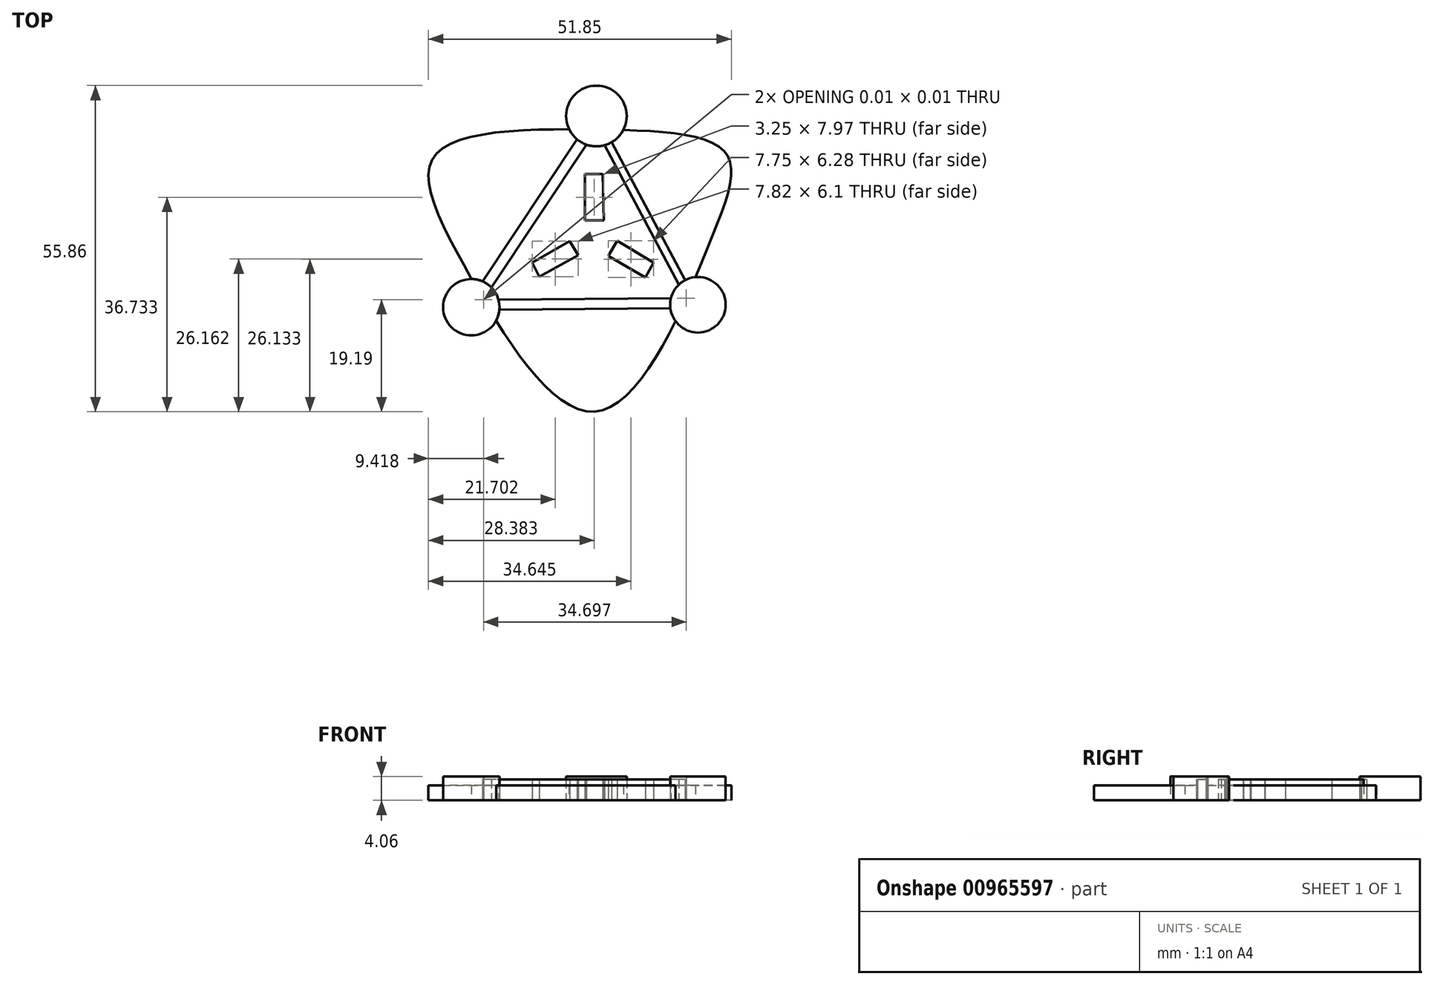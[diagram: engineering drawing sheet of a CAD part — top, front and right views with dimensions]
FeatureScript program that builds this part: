
annotation { "Feature Type Name" : "Feature", "Feature Type Description" : "" }
export const myFeature = defineFeature(function(context is Context, id is Id, definition is map)
    precondition{}
    {
        {
            var Q0;
            Q0=qCreatedBy(makeId("Top.planeOp"),FACE);
            var sketch = newSketch(context, id + "F0", { "sketchPlane" : qUnion([Q0])});
            skFitSpline(sketch, "E0", {"points": [v(-33.67, 21.37) * mm, v(-6.09, 25.74) * mm, v(15.95, 21.83) * mm, v(13.28, 6.3) * mm, v(-6.1, -22.56) * mm, v(-28.52, 2.03) * mm, v(-33.67, 21.37) * mm]});
            skLineSegment(sketch, "E1", {"start": v(-6.09, 25.74) * mm, "end": v(-25.43, -3.42) * mm});
            skLineSegment(sketch, "E2", {"start": v(9.28, -3.15) * mm, "end": v(-6.09, 25.74) * mm});
            skLineSegment(sketch, "E3", {"start": v(-25.43, -3.42) * mm, "end": v(9.28, -3.15) * mm});
            skCircle(sketch, "E4", {"center": v(-6.09, 28.06) * mm, "radius": 5.2 * mm});
            skCircle(sketch, "E5", {"center": v(11.28, -4.28) * mm, "radius": 4.76 * mm});
            skCircle(sketch, "E6", {"center": v(-27.5, -4.7) * mm, "radius": 4.83 * mm});
            skLineSegment(sketch, "E7", {"start": v(-8.08, 18.12) * mm, "end": v(-8.08, 10.15) * mm});
            skLineSegment(sketch, "E8", {"start": v(-8.08, 10.15) * mm, "end": v(-4.83, 10.15) * mm});
            skLineSegment(sketch, "E9", {"start": v(-4.83, 10.15) * mm, "end": v(-5, 18.09) * mm});
            skLineSegment(sketch, "E10", {"start": v(-5, 18.09) * mm, "end": v(-8.08, 18.12) * mm});
            skLineSegment(sketch, "E11", {"start": v(-17.05, 2.95) * mm, "end": v(-10.66, 6.61) * mm});
            skLineSegment(sketch, "E12", {"start": v(-10.66, 6.61) * mm, "end": v(-9.23, 4.24) * mm});
            skLineSegment(sketch, "E13", {"start": v(-9.23, 4.24) * mm, "end": v(-15.87, 0.51) * mm});
            skLineSegment(sketch, "E14", {"start": v(-15.87, 0.51) * mm, "end": v(-17.05, 2.95) * mm});
            skLineSegment(sketch, "E15", {"start": v(-2.56, 6.67) * mm, "end": v(-4.07, 4.1) * mm});
            skLineSegment(sketch, "E16", {"start": v(-4.07, 4.1) * mm, "end": v(2.26, 0.4) * mm});
            skLineSegment(sketch, "E17", {"start": v(2.26, 0.4) * mm, "end": v(3.68, 2.96) * mm});
            skLineSegment(sketch, "E18", {"start": v(3.68, 2.96) * mm, "end": v(-2.56, 6.67) * mm});
            skLineSegment(sketch, "E19", {"start": v(-8.28, 25.76) * mm, "end": v(-26.46, -1.63) * mm});
            skLineSegment(sketch, "E20", {"start": v(-26.46, -1.63) * mm, "end": v(-24.42, -5.12) * mm});
            skLineSegment(sketch, "E21", {"start": v(-24.42, -5.12) * mm, "end": v(8.5, -4.86) * mm});
            skLineSegment(sketch, "E22", {"start": v(8.5, -4.86) * mm, "end": v(9.95, -1.63) * mm});
            skLineSegment(sketch, "E23", {"start": v(9.95, -1.63) * mm, "end": v(-3.46, 23.57) * mm});
            skSolve(sketch);
        }
        {
            var Q0;
            Q0=makeQuery(id+"F0.imprint","IMPRINT",FACE,{"disambiguationData":[TD([[makeQuery(id+"F0.imprint","IMPRINT",EDGE,{"derivedFrom":sQuery(id+"F0.wireOp",EDGE,"E7")}),-1.0]])]});
            var Q1;
            {var subQ1=sQuery(id+"F0.wireOp",EDGE,"E2");var subQ3=sQuery(id+"F0.wireOp",EDGE,"E5");var subQ4=makeQuery(id+"F0.imprint","INTERSECT",VERTEX,{"derivedFrom":[subQ1,subQ3]});Q1=makeQuery(id+"F0.imprint","IMPRINT",FACE,{"disambiguationData":[TD([[makeQuery(id+"F0.imprint","IMPRINT",EDGE,{"disambiguationData":[TD([[subQ4,-1.0]])],"derivedFrom":subQ3}),1.0]])]});}
            var Q2;
            {var subQ1=sQuery(id+"F0.wireOp",EDGE,"E1");var subQ3=sQuery(id+"F0.wireOp",EDGE,"E6");var subQ4=makeQuery(id+"F0.imprint","INTERSECT",VERTEX,{"derivedFrom":[subQ1,subQ3]});Q2=makeQuery(id+"F0.imprint","IMPRINT",FACE,{"disambiguationData":[TD([[makeQuery(id+"F0.imprint","IMPRINT",EDGE,{"disambiguationData":[TD([[subQ4,1.0]])],"derivedFrom":subQ3}),1.0]])]});}
            var Q3;
            {var subQ0=sQuery(id+"F0.wireOp",EDGE,"E4");var subQ1=sQuery(id+"F0.wireOp",EDGE,"E0");var subQ2=makeQuery(id+"F0.imprint","INTERSECT",VERTEX,{"disambiguationData":[OD(1.0)],"derivedFrom":[subQ1,subQ0]});Q3=makeQuery(id+"F0.imprint","IMPRINT",FACE,{"disambiguationData":[TD([[makeQuery(id+"F0.imprint","IMPRINT",EDGE,{"disambiguationData":[TD([[subQ2,-1.0]])],"derivedFrom":subQ1}),-1.0]])]});}
            var Q4;
            {var subQ0=sQuery(id+"F0.wireOp",EDGE,"E5");var subQ1=sQuery(id+"F0.wireOp",EDGE,"E0");var subQ2=makeQuery(id+"F0.imprint","INTERSECT",VERTEX,{"disambiguationData":[OD(1.0)],"derivedFrom":[subQ1,subQ0]});Q4=makeQuery(id+"F0.imprint","IMPRINT",FACE,{"disambiguationData":[TD([[makeQuery(id+"F0.imprint","IMPRINT",EDGE,{"disambiguationData":[TD([[subQ2,-1.0]])],"derivedFrom":subQ1}),-1.0]])]});}
            var Q5;
            {var subQ0=sQuery(id+"F0.wireOp",EDGE,"E4");var subQ1=sQuery(id+"F0.wireOp",EDGE,"E0");var subQ2=makeQuery(id+"F0.imprint","INTERSECT",VERTEX,{"disambiguationData":[OD(0.0)],"derivedFrom":[subQ1,subQ0]});Q5=makeQuery(id+"F0.imprint","IMPRINT",FACE,{"disambiguationData":[TD([[makeQuery(id+"F0.imprint","IMPRINT",EDGE,{"disambiguationData":[TD([[subQ2,1.0]])],"derivedFrom":subQ1}),-1.0]])]});}
            extrude(context, id + "F1", {"entities" : qUnion([Q0, Q1, Q2, Q3, Q4, Q5]), "depth" : 2.54 * mm, "offsetDistance" : 25.4 * mm});
        }
        {
            var Q0;
            {var subQ0=sQuery(id+"F0.wireOp",EDGE,"E4");var subQ1=sQuery(id+"F0.wireOp",EDGE,"E1");var subQ2=makeQuery(id+"F0.imprint","INTERSECT",VERTEX,{"derivedFrom":[subQ1,subQ0]});Q0=makeQuery(id+"F0.imprint","IMPRINT",FACE,{"disambiguationData":[TD([[makeQuery(id+"F0.imprint","IMPRINT",EDGE,{"disambiguationData":[TD([[subQ2,-1.0]])],"derivedFrom":subQ1}),-1.0]])]});}
            var Q1;
            {var subQ0=sQuery(id+"F0.wireOp",EDGE,"E5");var subQ1=sQuery(id+"F0.wireOp",EDGE,"E2");var subQ2=makeQuery(id+"F0.imprint","INTERSECT",VERTEX,{"derivedFrom":[subQ1,subQ0]});Q1=makeQuery(id+"F0.imprint","IMPRINT",FACE,{"disambiguationData":[TD([[makeQuery(id+"F0.imprint","IMPRINT",EDGE,{"disambiguationData":[TD([[subQ2,-1.0]])],"derivedFrom":subQ1}),-1.0]])]});}
            var Q2;
            {var subQ0=sQuery(id+"F0.wireOp",EDGE,"E6");var subQ1=sQuery(id+"F0.wireOp",EDGE,"E3");var subQ2=makeQuery(id+"F0.imprint","INTERSECT",VERTEX,{"derivedFrom":[subQ1,subQ0]});Q2=makeQuery(id+"F0.imprint","IMPRINT",FACE,{"disambiguationData":[TD([[makeQuery(id+"F0.imprint","IMPRINT",EDGE,{"disambiguationData":[TD([[subQ2,-1.0]])],"derivedFrom":subQ1}),-1.0]])]});}
            var Q3;
            Q3=makeQuery(id+"F0.imprint","IMPRINT",FACE,{"disambiguationData":[TD([[makeQuery(id+"F0.imprint","IMPRINT",EDGE,{"derivedFrom":sQuery(id+"F0.wireOp",EDGE,"E7")}),1.0]])]});
            var Q4;
            Q4=makeQuery(id+"F0.imprint","IMPRINT",FACE,{"disambiguationData":[TD([[makeQuery(id+"F0.imprint","IMPRINT",EDGE,{"derivedFrom":sQuery(id+"F0.wireOp",EDGE,"E15")}),1.0]])]});
            var Q5;
            Q5=makeQuery(id+"F0.imprint","IMPRINT",FACE,{"disambiguationData":[TD([[makeQuery(id+"F0.imprint","IMPRINT",EDGE,{"derivedFrom":sQuery(id+"F0.wireOp",EDGE,"E11")}),-1.0]])]});
            extrude(context, id + "F2", {"entities" : qUnion([Q0, Q1, Q2, Q3, Q4, Q5]), "depth" : 3.56 * mm, "offsetDistance" : 25.4 * mm});
        }
        {
            var Q0;
            {var subQ0=sQuery(id+"F0.wireOp",EDGE,"E0");var subQ1=makeQuery(id+"F0.imprint","INTERSECT",VERTEX,{"derivedFrom":[subQ0,sQuery(id+"F0.wireOp",EDGE,"E19")]});Q0=makeQuery(id+"F0.imprint","IMPRINT",FACE,{"disambiguationData":[TD([[makeQuery(id+"F0.imprint","IMPRINT",EDGE,{"disambiguationData":[TD([[subQ1,1.0]])],"derivedFrom":subQ0}),1.0]])]});}
            var Q1;
            {var subQ3=sQuery(id+"F0.wireOp",EDGE,"E4");var subQ6=makeQuery(id+"F0.imprint","INTERSECT",VERTEX,{"derivedFrom":[subQ3,sQuery(id+"F0.wireOp",EDGE,"E23")]});Q1=makeQuery(id+"F0.imprint","IMPRINT",FACE,{"disambiguationData":[TD([[makeQuery(id+"F0.imprint","IMPRINT",EDGE,{"disambiguationData":[TD([[subQ6,1.0]])],"derivedFrom":subQ3}),1.0]])]});}
            var Q2;
            {var subQ0=sQuery(id+"F0.wireOp",EDGE,"E1");var subQ5=sQuery(id+"F0.wireOp",EDGE,"E4");var subQ6=makeQuery(id+"F0.imprint","INTERSECT",VERTEX,{"derivedFrom":[subQ0,subQ5]});Q2=makeQuery(id+"F0.imprint","IMPRINT",FACE,{"disambiguationData":[TD([[makeQuery(id+"F0.imprint","IMPRINT",EDGE,{"disambiguationData":[TD([[subQ6,1.0]])],"derivedFrom":subQ5}),1.0]])]});}
            var Q3;
            {var subQ0=sQuery(id+"F0.wireOp",EDGE,"E19");var subQ1=sQuery(id+"F0.wireOp",EDGE,"E0");var subQ2=makeQuery(id+"F0.imprint","INTERSECT",VERTEX,{"derivedFrom":[subQ1,subQ0]});Q3=makeQuery(id+"F0.imprint","IMPRINT",FACE,{"disambiguationData":[TD([[makeQuery(id+"F0.imprint","IMPRINT",EDGE,{"disambiguationData":[TD([[subQ2,1.0]])],"derivedFrom":subQ1}),-1.0]])]});}
            var Q4;
            {var subQ1=sQuery(id+"F0.wireOp",EDGE,"E1");var subQ3=sQuery(id+"F0.wireOp",EDGE,"E4");var subQ4=makeQuery(id+"F0.imprint","INTERSECT",VERTEX,{"derivedFrom":[subQ1,subQ3]});Q4=makeQuery(id+"F0.imprint","IMPRINT",FACE,{"disambiguationData":[TD([[makeQuery(id+"F0.imprint","IMPRINT",EDGE,{"disambiguationData":[TD([[subQ4,-1.0]])],"derivedFrom":subQ3}),1.0]])]});}
            var Q5;
            {var subQ1=sQuery(id+"F0.wireOp",EDGE,"E0");var subQ3=sQuery(id+"F0.wireOp",EDGE,"E5");var subQ7=makeQuery(id+"F0.imprint","INTERSECT",VERTEX,{"disambiguationData":[OD(0.0)],"derivedFrom":[subQ1,subQ3]});Q5=makeQuery(id+"F0.imprint","IMPRINT",FACE,{"disambiguationData":[TD([[makeQuery(id+"F0.imprint","IMPRINT",EDGE,{"disambiguationData":[TD([[subQ7,1.0]])],"derivedFrom":subQ3}),1.0]])]});}
            var Q6;
            {var subQ1=sQuery(id+"F0.wireOp",EDGE,"E0");var subQ3=sQuery(id+"F0.wireOp",EDGE,"E5");var subQ4=makeQuery(id+"F0.imprint","INTERSECT",VERTEX,{"disambiguationData":[OD(0.0)],"derivedFrom":[subQ1,subQ3]});Q6=makeQuery(id+"F0.imprint","IMPRINT",FACE,{"disambiguationData":[TD([[makeQuery(id+"F0.imprint","IMPRINT",EDGE,{"disambiguationData":[TD([[subQ4,-1.0]])],"derivedFrom":subQ3}),1.0]])]});}
            var Q7;
            {var subQ0=sQuery(id+"F0.wireOp",EDGE,"E22");var subQ1=sQuery(id+"F0.wireOp",EDGE,"E2");var subQ2=makeQuery(id+"F0.imprint","INTERSECT",VERTEX,{"derivedFrom":[subQ1,subQ0]});Q7=makeQuery(id+"F0.imprint","IMPRINT",FACE,{"disambiguationData":[TD([[makeQuery(id+"F0.imprint","IMPRINT",EDGE,{"disambiguationData":[TD([[subQ2,-1.0]])],"derivedFrom":subQ1}),-1.0]])]});}
            var Q8;
            {var subQ0=sQuery(id+"F0.wireOp",EDGE,"E22");var subQ1=sQuery(id+"F0.wireOp",EDGE,"E2");var subQ2=makeQuery(id+"F0.imprint","INTERSECT",VERTEX,{"derivedFrom":[subQ1,subQ0]});Q8=makeQuery(id+"F0.imprint","IMPRINT",FACE,{"disambiguationData":[TD([[makeQuery(id+"F0.imprint","IMPRINT",EDGE,{"disambiguationData":[TD([[subQ2,-1.0]])],"derivedFrom":subQ1}),1.0]])]});}
            var Q9;
            {var subQ0=sQuery(id+"F0.wireOp",EDGE,"E5");var subQ1=sQuery(id+"F0.wireOp",EDGE,"E3");var subQ2=makeQuery(id+"F0.imprint","INTERSECT",VERTEX,{"derivedFrom":[subQ1,subQ0]});Q9=makeQuery(id+"F0.imprint","IMPRINT",FACE,{"disambiguationData":[TD([[makeQuery(id+"F0.imprint","IMPRINT",EDGE,{"disambiguationData":[TD([[subQ2,-1.0]])],"derivedFrom":subQ1}),-1.0]])]});}
            var Q10;
            {var subQ1=sQuery(id+"F0.wireOp",EDGE,"E0");var subQ3=sQuery(id+"F0.wireOp",EDGE,"E5");var subQ4=makeQuery(id+"F0.imprint","INTERSECT",VERTEX,{"disambiguationData":[OD(1.0)],"derivedFrom":[subQ1,subQ3]});Q10=makeQuery(id+"F0.imprint","IMPRINT",FACE,{"disambiguationData":[TD([[makeQuery(id+"F0.imprint","IMPRINT",EDGE,{"disambiguationData":[TD([[subQ4,1.0]])],"derivedFrom":subQ3}),1.0]])]});}
            var Q11;
            {var subQ1=sQuery(id+"F0.wireOp",EDGE,"E0");var subQ3=sQuery(id+"F0.wireOp",EDGE,"E6");var subQ7=makeQuery(id+"F0.imprint","INTERSECT",VERTEX,{"disambiguationData":[OD(0.0)],"derivedFrom":[subQ1,subQ3]});Q11=makeQuery(id+"F0.imprint","IMPRINT",FACE,{"disambiguationData":[TD([[makeQuery(id+"F0.imprint","IMPRINT",EDGE,{"disambiguationData":[TD([[subQ7,1.0]])],"derivedFrom":subQ3}),1.0]])]});}
            var Q12;
            {var subQ1=sQuery(id+"F0.wireOp",EDGE,"E0");var subQ3=sQuery(id+"F0.wireOp",EDGE,"E6");var subQ4=makeQuery(id+"F0.imprint","INTERSECT",VERTEX,{"disambiguationData":[OD(1.0)],"derivedFrom":[subQ1,subQ3]});Q12=makeQuery(id+"F0.imprint","IMPRINT",FACE,{"disambiguationData":[TD([[makeQuery(id+"F0.imprint","IMPRINT",EDGE,{"disambiguationData":[TD([[subQ4,1.0]])],"derivedFrom":subQ3}),1.0]])]});}
            var Q13;
            {var subQ0=sQuery(id+"F0.wireOp",EDGE,"E6");var subQ1=sQuery(id+"F0.wireOp",EDGE,"E1");var subQ2=makeQuery(id+"F0.imprint","INTERSECT",VERTEX,{"derivedFrom":[subQ1,subQ0]});Q13=makeQuery(id+"F0.imprint","IMPRINT",FACE,{"disambiguationData":[TD([[makeQuery(id+"F0.imprint","IMPRINT",EDGE,{"disambiguationData":[TD([[subQ2,-1.0]])],"derivedFrom":subQ1}),-1.0]])]});}
            var Q14;
            {var subQ0=sQuery(id+"F0.wireOp",EDGE,"E6");var subQ1=sQuery(id+"F0.wireOp",EDGE,"E1");var subQ2=makeQuery(id+"F0.imprint","INTERSECT",VERTEX,{"derivedFrom":[subQ1,subQ0]});Q14=makeQuery(id+"F0.imprint","IMPRINT",FACE,{"disambiguationData":[TD([[makeQuery(id+"F0.imprint","IMPRINT",EDGE,{"disambiguationData":[TD([[subQ2,-1.0]])],"derivedFrom":subQ1}),1.0]])]});}
            var Q15;
            {var subQ0=sQuery(id+"F0.wireOp",EDGE,"E20");var subQ1=sQuery(id+"F0.wireOp",EDGE,"E3");var subQ2=makeQuery(id+"F0.imprint","INTERSECT",VERTEX,{"derivedFrom":[subQ1,subQ0]});Q15=makeQuery(id+"F0.imprint","IMPRINT",FACE,{"disambiguationData":[TD([[makeQuery(id+"F0.imprint","IMPRINT",EDGE,{"disambiguationData":[TD([[subQ2,-1.0]])],"derivedFrom":subQ1}),-1.0]])]});}
            var Q16;
            {var subQ1=sQuery(id+"F0.wireOp",EDGE,"E0");var subQ3=sQuery(id+"F0.wireOp",EDGE,"E6");var subQ4=makeQuery(id+"F0.imprint","INTERSECT",VERTEX,{"disambiguationData":[OD(0.0)],"derivedFrom":[subQ1,subQ3]});Q16=makeQuery(id+"F0.imprint","IMPRINT",FACE,{"disambiguationData":[TD([[makeQuery(id+"F0.imprint","IMPRINT",EDGE,{"disambiguationData":[TD([[subQ4,-1.0]])],"derivedFrom":subQ3}),1.0]])]});}
            var Q17;
            {var subQ0=sQuery(id+"F0.wireOp",EDGE,"E1");var subQ3=sQuery(id+"F0.wireOp",EDGE,"E20");var subQ5=makeQuery(id+"F0.imprint","INTERSECT",VERTEX,{"derivedFrom":[subQ0,subQ3]});Q17=makeQuery(id+"F0.imprint","IMPRINT",FACE,{"disambiguationData":[TD([[makeQuery(id+"F0.imprint","IMPRINT",EDGE,{"disambiguationData":[TD([[subQ5,-1.0]])],"derivedFrom":subQ0}),-1.0]])]});}
            var Q18;
            {var subQ0=sQuery(id+"F0.wireOp",EDGE,"E3");var subQ3=sQuery(id+"F0.wireOp",EDGE,"E20");var subQ5=makeQuery(id+"F0.imprint","INTERSECT",VERTEX,{"derivedFrom":[subQ0,subQ3]});Q18=makeQuery(id+"F0.imprint","IMPRINT",FACE,{"disambiguationData":[TD([[makeQuery(id+"F0.imprint","IMPRINT",EDGE,{"disambiguationData":[TD([[subQ5,1.0]])],"derivedFrom":subQ0}),-1.0]])]});}
            var Q19;
            {var subQ0=sQuery(id+"F0.wireOp",EDGE,"E3");var subQ3=sQuery(id+"F0.wireOp",EDGE,"E22");var subQ5=makeQuery(id+"F0.imprint","INTERSECT",VERTEX,{"derivedFrom":[subQ0,subQ3]});Q19=makeQuery(id+"F0.imprint","IMPRINT",FACE,{"disambiguationData":[TD([[makeQuery(id+"F0.imprint","IMPRINT",EDGE,{"disambiguationData":[TD([[subQ5,-1.0]])],"derivedFrom":subQ0}),-1.0]])]});}
            var Q20;
            {var subQ0=sQuery(id+"F0.wireOp",EDGE,"E2");var subQ3=sQuery(id+"F0.wireOp",EDGE,"E22");var subQ5=makeQuery(id+"F0.imprint","INTERSECT",VERTEX,{"derivedFrom":[subQ0,subQ3]});Q20=makeQuery(id+"F0.imprint","IMPRINT",FACE,{"disambiguationData":[TD([[makeQuery(id+"F0.imprint","IMPRINT",EDGE,{"disambiguationData":[TD([[subQ5,1.0]])],"derivedFrom":subQ0}),-1.0]])]});}
            extrude(context, id + "F3", {"entities" : qUnion([Q0, Q1, Q2, Q3, Q4, Q5, Q6, Q7, Q8, Q9, Q10, Q11, Q12, Q13, Q14, Q15, Q16, Q17, Q18, Q19, Q20]), "depth" : 4.06 * mm, "offsetDistance" : 25.4 * mm});
        }
    });
